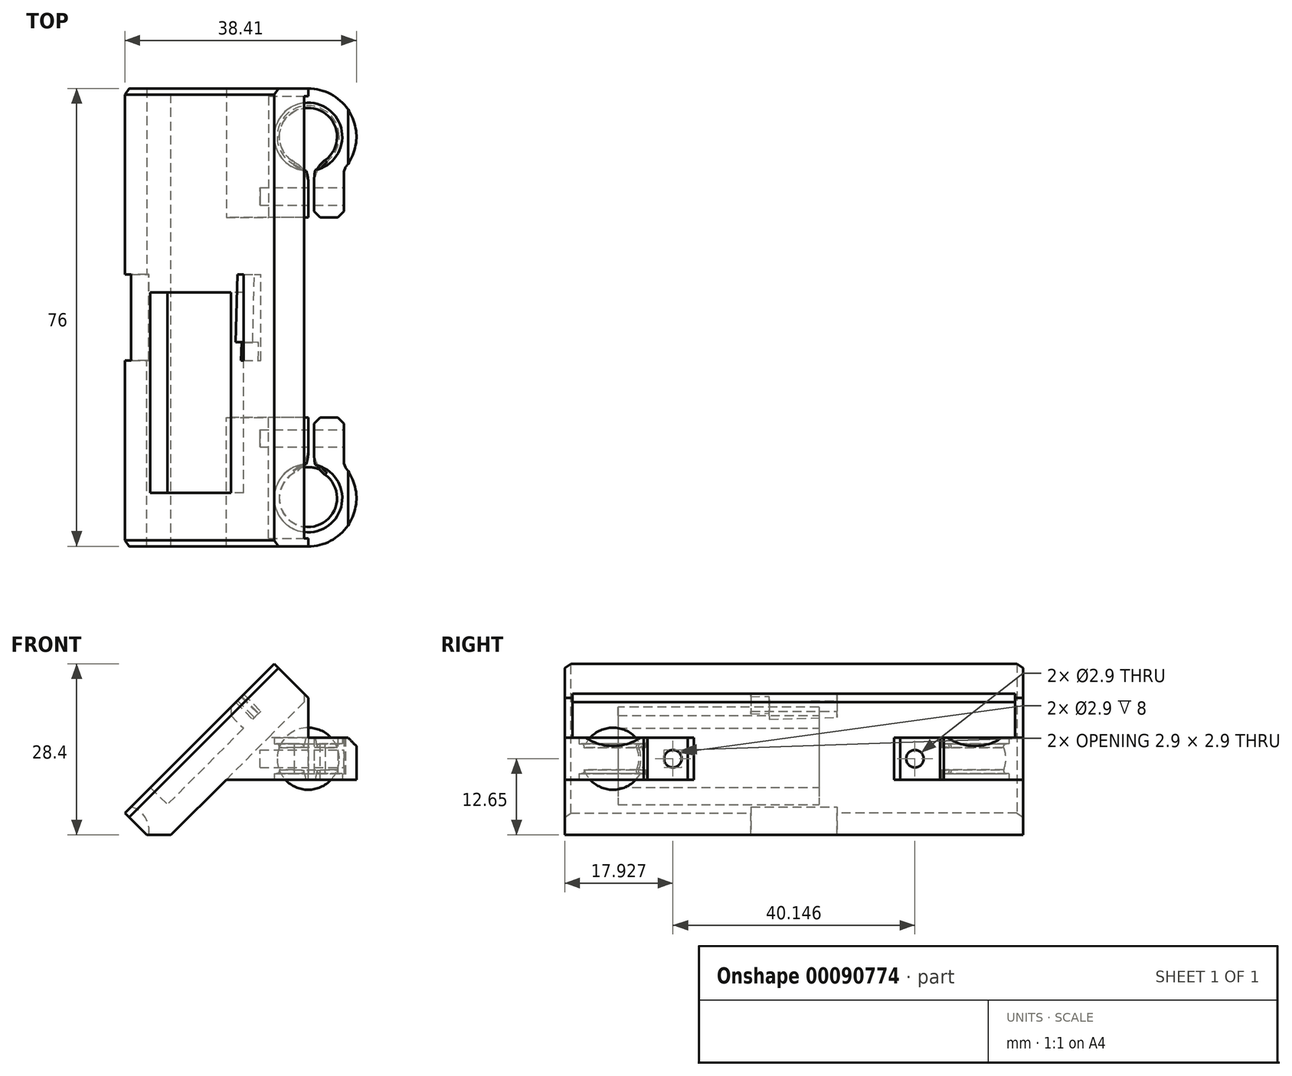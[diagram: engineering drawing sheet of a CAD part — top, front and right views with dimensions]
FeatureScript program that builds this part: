
annotation { "Feature Type Name" : "Feature", "Feature Type Description" : "" }
export const myFeature = defineFeature(function(context is Context, id is Id, definition is map)
    precondition{}
    {
        {
            assignVariable(context, id + "F0", {"name" : "balld", "anyValue" : 10});
        }
        {
            assignVariable(context, id + "F1", {"name" : "bushd", "anyValue" : 8});
        }
        {
            var Q0;
            Q0=qCreatedBy(makeId("Top.planeOp"),FACE);
            var sketch = newSketch(context, id + "F2", { "sketchPlane" : qUnion([Q0])});
            skLineSegment(sketch, "E0", {"start": v(0, -30) * mm, "end": v(0, 30) * mm});
            skCircle(sketch, "E1", {"center": v(0, -30) * mm, "radius": 5.15 * mm});
            skArc(sketch, "E2", {"start": v(0, -38) * mm, "mid": v(7.31, -33.24) * mm, "end": v(5.92, -24.62) * mm});
            skLineSegment(sketch, "E3", {"start": v(-5.15, -30) * mm, "end": v(5.15, -30) * mm});
            skLineSegment(sketch, "E4", {"start": v(-8, -30) * mm, "end": v(-8, 0) * mm});
            skLineSegment(sketch, "E5", {"start": v(-8, 0) * mm, "end": v(0, 0) * mm});
            skLineSegment(sketch, "E6", {"start": v(0, -16.62) * mm, "end": v(5.92, -16.62) * mm});
            skLineSegment(sketch, "E7", {"start": v(5.92, -16.62) * mm, "end": v(5.92, -24.62) * mm});
            skLineSegment(sketch, "E8", {"start": v(1, -30) * mm, "end": v(1, -16.62) * mm});
            skCircle(sketch, "E9.0", {"center": v(0, -30) * mm, "radius": 5.65 * mm});
            skLineSegment(sketch, "E10", {"start": v(-8, -30) * mm, "end": v(-8, -38) * mm});
            skLineSegment(sketch, "E11", {"start": v(-8, -38) * mm, "end": v(2.55, -38) * mm});
            skSolve(sketch);
        }
        {
            var Q0;
            Q0=makeQuery(id+"F2.imprint","IMPRINT",FACE,{"disambiguationData":[TD([[makeQuery(id+"F2.imprint","IMPRINT",EDGE,{"derivedFrom":sQuery(id+"F2.wireOp",EDGE,"E2")}),1.0]])]});
            var Q1;
            {var subQ0=sQuery(id+"F2.wireOp",EDGE,"E3");Q1=makeQuery(id+"F2.imprint","IMPRINT",FACE,{"disambiguationData":[TD([[makeQuery(id+"F2.imprint","IMPRINT",EDGE,{"derivedFrom":subQ0}),1.0]])]});}
            var Q2;
            {var subQ0=sQuery(id+"F2.wireOp",EDGE,"E3");Q2=makeQuery(id+"F2.imprint","IMPRINT",FACE,{"disambiguationData":[TD([[makeQuery(id+"F2.imprint","IMPRINT",EDGE,{"derivedFrom":subQ0}),-1.0]])]});}
            var Q3;
            {var subQ0=sQuery(id+"F2.wireOp",EDGE,"0A8tKCgS-ejaw-YyMs-Dn46-rruMUtFQQFLV");Q3=makeQuery(id+"F2.imprint","IMPRINT",FACE,{"disambiguationData":[TD([[makeQuery(id+"F2.imprint","IMPRINT",EDGE,{"derivedFrom":subQ0}),1.0]])]});}
            var Q4;
            {var subQ1=sQuery(id+"F2.wireOp",EDGE,"E1");var subQ8=sQuery(id+"F2.wireOp",EDGE,"E0");var subQ9=makeQuery(id+"F2.imprint","INTERSECT",VERTEX,{"derivedFrom":[subQ8,subQ1]});Q4=makeQuery(id+"F2.imprint","IMPRINT",FACE,{"disambiguationData":[TD([[makeQuery(id+"F2.imprint","IMPRINT",EDGE,{"disambiguationData":[TD([[subQ9,-1.0]])],"derivedFrom":subQ8}),1.0]])]});}
            extrude(context, id + "F3", {"entities" : qUnion([Q0, Q1, Q2, Q3, Q4]), "endBound" : BoundingType.SYMMETRIC, "depth" : (getVariable(context, 'balld') / 2) * mm});
        }
        {
            var Q0;
            {var subQ0=sQuery(id+"F2.wireOp",EDGE,"E3");var subQ1=sQuery(id+"F2.wireOp",EDGE,"E1");var subQ2=makeQuery(id+"F2.imprint","INTERSECT",VERTEX,{"disambiguationData":[OD(0.0)],"derivedFrom":[subQ1,subQ0]});Q0=makeQuery(id+"F2.imprint","IMPRINT",FACE,{"disambiguationData":[TD([[makeQuery(id+"F2.imprint","IMPRINT",EDGE,{"disambiguationData":[TD([[subQ2,-1.0]])],"derivedFrom":subQ1}),1.0]])]});}
            var Q1;
            Q1=sQuery(id+"F2.wireOp",EDGE,"E3");
            revolve(context, id + "F4", {"operationType" : NewBodyOperationType.REMOVE, "entities" : qUnion([Q0]), "axis" : qUnion([Q1]), "revolveType" : RevolveType.FULL, "oppositeDirection" : true});
        }
        {
            var Q0;
            Q0=makeQuery(id+"F2.imprint","IMPRINT",FACE,{"disambiguationData":[TD([[makeQuery(id+"F2.imprint","IMPRINT",EDGE,{"derivedFrom":sQuery(id+"F2.wireOp",EDGE,"E2")}),1.0]])]});
            extrude(context, id + "F5", {"entities" : qUnion([Q0]), "operationType" : NewBodyOperationType.ADD, "endBound" : BoundingType.SYMMETRIC, "depth" : 7 * mm});
        }
        {
            var Q0;
            {var subQ0=sQuery(id+"F2.wireOp",EDGE,"E3");var subQ1=sQuery(id+"F2.wireOp",EDGE,"E1");var subQ2=makeQuery(id+"F2.imprint","INTERSECT",VERTEX,{"disambiguationData":[OD(0.0)],"derivedFrom":[subQ1,subQ0]});Q0=makeQuery(id+"F2.imprint","IMPRINT",FACE,{"disambiguationData":[TD([[makeQuery(id+"F2.imprint","IMPRINT",EDGE,{"disambiguationData":[TD([[subQ2,-1.0]])],"derivedFrom":subQ1}),1.0]])]});}
            var Q1;
            Q1=sQuery(id+"F2.wireOp",EDGE,"E3");
            revolve(context, id + "F6", {"entities" : qUnion([Q0]), "axis" : qUnion([Q1]), "revolveType" : RevolveType.FULL});
        }
        {
            var Q0;
            Q0=makeQuery(id+"F4.boolean.opBoolean","INTERSECT",EDGE,{"derivedFrom":[makeQuery(id+"F3.opExtrude","SWEPT_FACE",FACE,{"disambiguationData":[OSD([sQuery(id+"F2.wireOp",EDGE,"E0")])]}),makeQuery(id+"F4.opRevolve","SWEPT_FACE",FACE,{"disambiguationData":[OSD([sQuery(id+"F2.wireOp",EDGE,"E1")])]})]});
            var Q1;
            Q1=makeQuery(id+"F4.boolean.opBoolean","INTERSECT",EDGE,{"derivedFrom":[makeQuery(id+"F3.opExtrude","SWEPT_FACE",FACE,{"disambiguationData":[OSD([sQuery(id+"F2.wireOp",EDGE,"E8")])]}),makeQuery(id+"F4.opRevolve","SWEPT_FACE",FACE,{"disambiguationData":[OSD([sQuery(id+"F2.wireOp",EDGE,"E1")])]})]});
            fillet(context, id + "F7", {"entities" : qUnion([Q0, Q1]), "radius" : 4 * mm, "tangentPropagation" : true, "allowEdgeOverflow" : false});
        }
        {
            var Q0;
            {var subQ0=sQuery(id+"F2.wireOp",EDGE,"E7");Q0=makeQuery(id+"F5.boolean.opBoolean","MERGE",FACE,{"derivedFrom":[makeQuery(id+"F3.opExtrude","SWEPT_FACE",FACE,{"disambiguationData":[OSD([subQ0])]}),makeQuery(id+"F5.opExtrude","SWEPT_FACE",FACE,{"disambiguationData":[OSD([subQ0])]})]});}
            var sketch = newSketch(context, id + "F8", { "sketchPlane" : qUnion([Q0])});
            skCircle(sketch, "E12", {"center": v(-20.07, 0) * mm, "radius": 1.45 * mm});
            skPoint(sketch, "E12.centerSnap0", {"position": v(-16.62, 0) * mm});
            skSolve(sketch);
        }
        {
            var Q0;
            Q0=makeQuery(id+"F8.imprint","IMPRINT",FACE,{"disambiguationData":[TD([[makeQuery(id+"F8.imprint","IMPRINT",EDGE,{"derivedFrom":sQuery(id+"F8.wireOp",EDGE,"E12")}),1.0]])]});
            extrude(context, id + "F9", {"entities" : qUnion([Q0]), "operationType" : NewBodyOperationType.REMOVE, "oppositeDirection" : true, "depth" : 25 * mm});
        }
        {
            var Q0;
            {var subQ0=sQuery(id+"F2.wireOp",EDGE,"E5");Q0=makeQuery(id+"F5.boolean.opBoolean","MERGE",FACE,{"derivedFrom":[makeQuery(id+"F3.opExtrude","SWEPT_FACE",FACE,{"disambiguationData":[OSD([subQ0])]}),makeQuery(id+"F5.opExtrude","SWEPT_FACE",FACE,{"disambiguationData":[OSD([subQ0])]})]});}
            var sketch = newSketch(context, id + "F10", { "sketchPlane" : qUnion([Q0])});
            skLineSegment(sketch, "E13", {"start": v(30.4, -9) * mm, "end": v(5.66, 15.75) * mm});
            skLineSegment(sketch, "E14", {"start": v(5.66, 15.75) * mm, "end": v(0, 10.1) * mm});
            skLineSegment(sketch, "E15", {"start": v(0, 10.1) * mm, "end": v(6.6, 3.5) * mm});
            skLineSegment(sketch, "E16", {"start": v(6.6, 3.5) * mm, "end": v(24.75, -14.65) * mm});
            skLineSegment(sketch, "E17", {"start": v(30.4, -9) * mm, "end": v(24.75, -14.65) * mm});
            skLineSegment(sketch, "E18", {"start": v(26.75, -12.65) * mm, "end": v(22.75, -12.65) * mm});
            skLineSegment(sketch, "E19", {"start": v(8, -3.5) * mm, "end": v(13.6, -3.5) * mm});
            skLineSegment(sketch, "E20", {"start": v(-8, -3.5) * mm, "end": v(-8, 3.5) * mm});
            skLineSegment(sketch, "E21", {"start": v(0, 10.1) * mm, "end": v(-10.1, 0) * mm});
            skLineSegment(sketch, "E22.0", {"start": v(-8, 3.5) * mm, "end": v(0, 3.5) * mm});
            skSolve(sketch);
        }
        {
            var Q0;
            {var subQ0=sQuery(id+"F10.wireOp",EDGE,"E14");Q0=makeQuery(id+"F10.imprint","IMPRINT",FACE,{"disambiguationData":[TD([[makeQuery(id+"F10.imprint","IMPRINT",EDGE,{"derivedFrom":subQ0}),1.0]])]});}
            var Q1;
            {var subQ0=sQuery(id+"F10.wireOp",EDGE,"ik6ux5z4-sAW3-eP5y-JmRx-WD4Mi1XPYjA4");var subQ5=sQuery(id+"F10.wireOp",EDGE,"E16");var subQ6=makeQuery(id+"F10.imprint","INTERSECT",VERTEX,{"derivedFrom":[subQ0,subQ5]});Q1=makeQuery(id+"F10.imprint","IMPRINT",FACE,{"disambiguationData":[TD([[makeQuery(id+"F10.imprint","IMPRINT",EDGE,{"disambiguationData":[TD([[subQ6,1.0]])],"derivedFrom":subQ5}),-1.0]])]});}
            var Q2;
            {var subQ0=sQuery(id+"F2.wireOp",EDGE,"E11");Q2=makeQuery(id+"F5.boolean.opBoolean","MERGE",FACE,{"derivedFrom":[makeQuery(id+"F3.opExtrude","SWEPT_FACE",FACE,{"disambiguationData":[OSD([subQ0])]}),makeQuery(id+"F5.opExtrude","SWEPT_FACE",FACE,{"disambiguationData":[OSD([subQ0])]})]});}
            extrude(context, id + "F11", {"entities" : qUnion([Q0, Q1]), "operationType" : NewBodyOperationType.ADD, "endBound" : BoundingType.UP_TO_SURFACE, "oppositeDirection" : true, "endBoundEntityFace" : qUnion([Q2]), "depth" : (30 + getVariable(context, 'bushd')) * mm});
        }
        {
            var Q0;
            {var subQ0=sQuery(id+"F2.wireOp",EDGE,"E5");var subQ3=makeQuery(id+"F5.opExtrude","CAP_EDGE",EDGE,{"disambiguationData":[OSD([subQ0])],"isStart":true});Q0=makeQuery(id+"F10.imprint","IMPRINT",FACE,{"disambiguationData":[TD([[makeQuery(id+"F10.imprint","IMPRINT",EDGE,{"derivedFrom":subQ3}),-1.0]])]});}
            var Q1;
            {var subQ0=sQuery(id+"F10.wireOp",EDGE,"ik6ux5z4-sAW3-eP5y-JmRx-WD4Mi1XPYjA4");var subQ5=sQuery(id+"F10.wireOp",EDGE,"E16");var subQ6=makeQuery(id+"F10.imprint","INTERSECT",VERTEX,{"derivedFrom":[subQ0,subQ5]});Q1=makeQuery(id+"F10.imprint","IMPRINT",FACE,{"disambiguationData":[TD([[makeQuery(id+"F10.imprint","IMPRINT",EDGE,{"disambiguationData":[TD([[subQ6,1.0]])],"derivedFrom":subQ5}),-1.0]])]});}
            var Q2;
            {var subQ0=sQuery(id+"F2.wireOp",EDGE,"E6");Q2=makeQuery(id+"F5.boolean.opBoolean","MERGE",FACE,{"derivedFrom":[makeQuery(id+"F3.opExtrude","SWEPT_FACE",FACE,{"disambiguationData":[OSD([subQ0])]}),makeQuery(id+"F5.opExtrude","SWEPT_FACE",FACE,{"disambiguationData":[OSD([subQ0])]})]});}
            extrude(context, id + "F12", {"entities" : qUnion([Q0, Q1]), "operationType" : NewBodyOperationType.REMOVE, "endBound" : BoundingType.UP_TO_SURFACE, "oppositeDirection" : true, "endBoundEntityFace" : qUnion([Q2]), "depth" : 25 * mm});
        }
        {
            var Q0;
            {var subQ0=sQuery(id+"F10.wireOp",EDGE,"E22.0");var subQ1=sQuery(id+"F10.wireOp",EDGE,"E20");var subQ2=makeQuery(id+"F10.imprint","INTERSECT",VERTEX,{"derivedFrom":[subQ1,subQ0]});Q0=makeQuery(id+"F10.imprint","IMPRINT",FACE,{"disambiguationData":[TD([[makeQuery(id+"F10.imprint","IMPRINT",EDGE,{"disambiguationData":[TD([[subQ2,1.0]])],"derivedFrom":subQ1}),-1.0]])]});}
            extrude(context, id + "F13", {"entities" : qUnion([Q0]), "operationType" : NewBodyOperationType.REMOVE, "oppositeDirection" : true, "depth" : 34.76 * mm});
        }
        {
            var Q0;
            {var subQ0=sQuery(id+"F2.wireOp",EDGE,"E11");Q0=makeQuery(id+"F11.boolean.opBoolean","MERGE",FACE,{"derivedFrom":[makeQuery(id+"F5.boolean.opBoolean","MERGE",FACE,{"derivedFrom":[makeQuery(id+"F3.opExtrude","SWEPT_FACE",FACE,{"disambiguationData":[OSD([subQ0])]}),makeQuery(id+"F5.opExtrude","SWEPT_FACE",FACE,{"disambiguationData":[OSD([subQ0])]})]}),makeQuery(id+"F11.opExtrude","CAP_FACE",FACE,{"disambiguationData":[OSD([sQuery(id+"F2.wireOp",EDGE,"E4"),sQuery(id+"F2.wireOp",EDGE,"E5"),sQuery(id+"F10.wireOp",EDGE,"ik6ux5z4-sAW3-eP5y-JmRx-WD4Mi1XPYjA4"),sQuery(id+"F10.wireOp",EDGE,"E13"),sQuery(id+"F10.wireOp",EDGE,"E14"),sQuery(id+"F10.wireOp",EDGE,"E15"),sQuery(id+"F10.wireOp",EDGE,"NVdRs6pZ-gfCu-PPoY-FiU9-BY5B9J22exEP")])],"isStart":false})]});}
            var sketch = newSketch(context, id + "F14", { "sketchPlane" : qUnion([Q0])});
            skLineSegment(sketch, "E23", {"start": v(0, 3.5) * mm, "end": v(0, 10.1) * mm});
            skSolve(sketch);
        }
        {
            var Q0;
            Q0=makeQuery(id+"F14.imprint","IMPRINT",FACE,{"disambiguationData":[TD([[makeQuery(id+"F14.imprint","IMPRINT",EDGE,{"derivedFrom":sQuery(id+"F14.wireOp",EDGE,"E23")}),1.0]])]});
            extrude(context, id + "F15", {"entities" : qUnion([Q0]), "operationType" : NewBodyOperationType.ADD, "oppositeDirection" : true, "depth" : 1.3 * mm});
        }
        {
            var Q0;
            Q0=makeQuery(id+"F4.boolean.opBoolean","INTERSECT",EDGE,{"derivedFrom":[makeQuery(id+"F3.opExtrude","CAP_FACE",FACE,{"disambiguationData":[OSD([sQuery(id+"F2.wireOp",EDGE,"E0"),sQuery(id+"F2.wireOp",EDGE,"E2"),sQuery(id+"F2.wireOp",EDGE,"E3"),sQuery(id+"F2.wireOp",EDGE,"E4"),sQuery(id+"F2.wireOp",EDGE,"E5"),sQuery(id+"F2.wireOp",EDGE,"E6"),sQuery(id+"F2.wireOp",EDGE,"E7"),sQuery(id+"F2.wireOp",EDGE,"E8")])],"isStart":true}),makeQuery(id+"F4.opRevolve","SWEPT_FACE",FACE,{"disambiguationData":[OSD([sQuery(id+"F2.wireOp",EDGE,"E1")])]})]});
            var Q1;
            Q1=makeQuery(id+"F4.boolean.opBoolean","INTERSECT",EDGE,{"derivedFrom":[makeQuery(id+"F3.opExtrude","CAP_FACE",FACE,{"disambiguationData":[OSD([sQuery(id+"F2.wireOp",EDGE,"E0"),sQuery(id+"F2.wireOp",EDGE,"E2"),sQuery(id+"F2.wireOp",EDGE,"E3"),sQuery(id+"F2.wireOp",EDGE,"E4"),sQuery(id+"F2.wireOp",EDGE,"E5"),sQuery(id+"F2.wireOp",EDGE,"E6"),sQuery(id+"F2.wireOp",EDGE,"E7"),sQuery(id+"F2.wireOp",EDGE,"E8")])],"isStart":false}),makeQuery(id+"F4.opRevolve","SWEPT_FACE",FACE,{"disambiguationData":[OSD([sQuery(id+"F2.wireOp",EDGE,"E1")])]})]});
            var Q2;
            Q2=makeQuery(id+"F11.opExtrude","SWEPT_EDGE",EDGE,{"disambiguationData":[OSD([sQuery(id+"F2.wireOp",EDGE,"E5"),sQuery(id+"F10.wireOp",EDGE,"E15"),sQuery(id+"F10.wireOp",EDGE,"E16")])]});
            var Q3;
            Q3=makeQuery(id+"F15.opExtrude","SWEPT_EDGE",EDGE,{"disambiguationData":[OSD([sQuery(id+"F2.wireOp",EDGE,"E2"),sQuery(id+"F2.wireOp",EDGE,"E11"),sQuery(id+"F14.wireOp",EDGE,"E23")])]});
            fillet(context, id + "F16", {"entities" : qUnion([Q0, Q1, Q2, Q3]), "radius" : 0.5 * mm, "tangentPropagation" : true, "allowEdgeOverflow" : false});
        }
        {
            var Q0;
            Q0=makeQuery(id+"F11.opExtrude","SWEPT_FACE",FACE,{"disambiguationData":[OSD([sQuery(id+"F10.wireOp",EDGE,"E13")])]});
            cPlane(context, id + "F17", {"entities" : qUnion([Q0]), "cplaneType" : CPlaneType.OFFSET, "offset" : 2 * mm, "oppositeDirection" : true, "width" : 150 * mm, "height" : 150 * mm});
        }
        {
            var Q0;
            Q0=qCreatedBy(id+"F17.planeOp",FACE);
            var sketch = newSketch(context, id + "F18", { "sketchPlane" : qUnion([Q0])});
            skLineSegment(sketch, "E24.bottom", {"start": v(7.14, -34.1) * mm, "end": v(-27.86, -34.1) * mm});
            skLineSegment(sketch, "E24.top", {"start": v(7.14, -25.9) * mm, "end": v(-27.86, -25.9) * mm});
            skLineSegment(sketch, "E24.left", {"start": v(7.14, -34.1) * mm, "end": v(7.14, -25.9) * mm});
            skLineSegment(sketch, "E24.right", {"start": v(-27.86, -34.1) * mm, "end": v(-27.86, -25.9) * mm});
            skPoint(sketch, "E24.middle", {"position": v(-10.36, -30) * mm});
            skPoint(sketch, "E24.middle.positionSnap0", {"position": v(-10.36, 0) * mm});
            skPoint(sketch, "E24.centerSnap0", {"position": v(-10.36, 0) * mm});
            skLineSegment(sketch, "E25", {"start": v(7.14, -30) * mm, "end": v(-27.86, -30) * mm});
            skLineSegment(sketch, "E26", {"start": v(7.14, -21.9) * mm, "end": v(-27.86, -21.9) * mm});
            skLineSegment(sketch, "E27.0.0", {"start": v(-27.86, -38) * mm, "end": v(7.14, -38) * mm});
            skLineSegment(sketch, "E27.0.1", {"start": v(7.14, -38) * mm, "end": v(7.14, 0) * mm});
            skLineSegment(sketch, "E27.0.2", {"start": v(7.14, 0) * mm, "end": v(-27.86, 0) * mm});
            skLineSegment(sketch, "E27.0.3", {"start": v(-27.86, 0) * mm, "end": v(-27.86, -38) * mm});
            skLineSegment(sketch, "E28", {"start": v(4.14, 0) * mm, "end": v(4.14, -21.9) * mm});
            skLineSegment(sketch, "E29", {"start": v(4.14, -4) * mm, "end": v(7.14, -4) * mm});
            skLineSegment(sketch, "E30", {"start": v(7.14, -4) * mm, "end": v(5.64, -4) * mm});
            skSolve(sketch);
        }
        {
            var Q0;
            {var subQ0=sQuery(id+"F18.wireOp",EDGE,"E24.top");Q0=makeQuery(id+"F18.imprint","IMPRINT",FACE,{"disambiguationData":[TD([[makeQuery(id+"F18.imprint","IMPRINT",EDGE,{"derivedFrom":subQ0}),1.0]])]});}
            var Q1;
            Q1=sQuery(id+"F18.wireOp",EDGE,"E25");
            revolve(context, id + "F19", {"operationType" : NewBodyOperationType.REMOVE, "entities" : qUnion([Q0]), "axis" : qUnion([Q1]), "revolveType" : RevolveType.FULL, "oppositeDirection" : true});
        }
        {
            var Q0;
            {var subQ3=sQuery(id+"F18.wireOp",EDGE,"E28");Q0=makeQuery(id+"F18.imprint","IMPRINT",FACE,{"disambiguationData":[TD([[makeQuery(id+"F18.imprint","IMPRINT",EDGE,{"derivedFrom":subQ3}),-1.0]])]});}
            var Q1;
            {var subQ5=sQuery(id+"F18.wireOp",EDGE,"E29");Q1=makeQuery(id+"F18.imprint","IMPRINT",FACE,{"disambiguationData":[TD([[makeQuery(id+"F18.imprint","IMPRINT",EDGE,{"derivedFrom":subQ5}),1.0]])]});}
            extrude(context, id + "F20", {"entities" : qUnion([Q0, Q1]), "operationType" : NewBodyOperationType.REMOVE, "depth" : 2 * mm, "hasSecondDirection" : true, "secondDirectionOppositeDirection" : true, "secondDirectionDepth" : 2 * mm});
        }
        {
            var Q0;
            Q0=makeQuery(id+"F3.opExtrude","SWEPT_BODY",BODY,{"disambiguationData":[OSD([sQuery(id+"F2.wireOp",EDGE,"E0"),sQuery(id+"F2.wireOp",EDGE,"E2"),sQuery(id+"F2.wireOp",EDGE,"E3"),sQuery(id+"F2.wireOp",EDGE,"E4"),sQuery(id+"F2.wireOp",EDGE,"E5"),sQuery(id+"F2.wireOp",EDGE,"E6"),sQuery(id+"F2.wireOp",EDGE,"E7"),sQuery(id+"F2.wireOp",EDGE,"E8"),sQuery(id+"F2.wireOp",EDGE,"E10"),sQuery(id+"F2.wireOp",EDGE,"E11")])]});
            var Q1;
            {var subQ0=sQuery(id+"F10.wireOp",EDGE,"E14");Q1=makeQuery(id+"F10.imprint","IMPRINT",FACE,{"disambiguationData":[TD([[makeQuery(id+"F10.imprint","IMPRINT",EDGE,{"derivedFrom":subQ0}),1.0]])]});}
            mirror(context, id + "F21", {"operationType" : NewBodyOperationType.ADD, "entities" : qUnion([Q0]), "mirrorPlane" : qUnion([Q1])});
        }
        {
            var Q0;
            {var subQ0=makeQuery(id+"F20.boolean.opBoolean","COPY",FACE,{"derivedFrom":makeQuery(id+"F20.opExtrude","CAP_FACE",FACE,{"disambiguationData":[OSD([sQuery(id+"F18.wireOp",EDGE,"E26"),sQuery(id+"F18.wireOp",EDGE,"E27.0.1"),sQuery(id+"F18.wireOp",EDGE,"E27.0.2"),sQuery(id+"F18.wireOp",EDGE,"E27.0.3")])],"isStart":true})});Q0=makeQuery(id+"F21.boolean.opBoolean","MERGE",FACE,{"derivedFrom":[subQ0,makeQuery(id+"F21.opPattern","COPY",FACE,{"derivedFrom":subQ0,"instanceName":"1"})]});}
            var sketch = newSketch(context, id + "F22", { "sketchPlane" : qUnion([Q0])});
            skLineSegment(sketch, "E31", {"start": v(7.14, 0) * mm, "end": v(-27.86, 0) * mm, "construction": true});
            skLineSegment(sketch, "E32", {"start": v(7.14, 0.7) * mm, "end": v(-24.81, 1.89) * mm});
            skLineSegment(sketch, "E33", {"start": v(7.14, -2) * mm, "end": v(-27.86, -0.7) * mm});
            skLineSegment(sketch, "E34", {"start": v(7.14, -0.6) * mm, "end": v(4.14, -0.49) * mm});
            skLineSegment(sketch, "E35", {"start": v(4.14, -0.49) * mm, "end": v(4.1, -1.89) * mm});
            skLineSegment(sketch, "E36.1.0", {"start": v(-27.86, 0.6) * mm, "end": v(-24.86, 0.49) * mm});
            skLineSegment(sketch, "E36.1.1", {"start": v(-24.86, 0.49) * mm, "end": v(-24.81, 1.89) * mm});
            skPoint(sketch, "E36.center", {"position": v(-10.36, 0) * mm});
            skLineSegment(sketch, "E37", {"start": v(-27.86, 4) * mm, "end": v(7.14, 4) * mm});
            skLineSegment(sketch, "E38.MirrorCS", {"start": v(-27.86, -4) * mm, "end": v(7.14, -4) * mm});
            skSolve(sketch);
        }
        {
            var Q0;
            {var subQ8=sQuery(id+"F22.wireOp",EDGE,"E37");Q0=makeQuery(id+"F22.imprint","IMPRINT",FACE,{"disambiguationData":[TD([[makeQuery(id+"F22.imprint","IMPRINT",EDGE,{"derivedFrom":subQ8}),-1.0]])]});}
            var Q1;
            {var subQ9=sQuery(id+"F22.wireOp",EDGE,"E36.1.0");Q1=makeQuery(id+"F22.imprint","IMPRINT",FACE,{"disambiguationData":[TD([[makeQuery(id+"F22.imprint","IMPRINT",EDGE,{"derivedFrom":subQ9}),1.0]])]});}
            var Q2;
            {var subQ0=sQuery(id+"F22.wireOp",EDGE,"E38.MirrorCS");Q2=makeQuery(id+"F22.imprint","IMPRINT",FACE,{"disambiguationData":[TD([[makeQuery(id+"F22.imprint","IMPRINT",EDGE,{"derivedFrom":subQ0}),1.0]])]});}
            var Q3;
            {var subQ5=sQuery(id+"F22.wireOp",EDGE,"E34");Q3=makeQuery(id+"F22.imprint","IMPRINT",FACE,{"disambiguationData":[TD([[makeQuery(id+"F22.imprint","IMPRINT",EDGE,{"derivedFrom":subQ5}),1.0]])]});}
            extrude(context, id + "F23", {"entities" : qUnion([Q0, Q1, Q2, Q3]), "operationType" : NewBodyOperationType.ADD, "depth" : 4 * mm});
        }
        {
            var Q0;
            Q0=makeQuery(id+"F20.boolean.opBoolean","COPY",EDGE,{"derivedFrom":makeQuery(id+"F20.opExtrude","CAP_EDGE",EDGE,{"disambiguationData":[OSD([sQuery(id+"F18.wireOp",EDGE,"E26")])],"isStart":false})});
            var Q1;
            Q1=makeQuery(id+"F11.opExtrude","CAP_EDGE",EDGE,{"disambiguationData":[OSD([sQuery(id+"F10.wireOp",EDGE,"E13")])],"isStart":false});
            var Q2;
            Q2=makeQuery(id+"F23.opExtrude","CAP_EDGE",EDGE,{"disambiguationData":[OSD([sQuery(id+"F22.wireOp",EDGE,"E38.MirrorCS")])],"isStart":false});
            var Q3;
            Q3=makeQuery(id+"F23.opExtrude","CAP_EDGE",EDGE,{"disambiguationData":[OSD([sQuery(id+"F22.wireOp",EDGE,"E37")])],"isStart":false});
            var Q4;
            Q4=makeQuery(id+"F21.opPattern","COPY",EDGE,{"derivedFrom":makeQuery(id+"F20.boolean.opBoolean","COPY",EDGE,{"derivedFrom":makeQuery(id+"F20.opExtrude","CAP_EDGE",EDGE,{"disambiguationData":[OSD([sQuery(id+"F18.wireOp",EDGE,"E26")])],"isStart":false})}),"instanceName":"1"});
            var Q5;
            Q5=makeQuery(id+"F21.opPattern","COPY",EDGE,{"derivedFrom":makeQuery(id+"F11.opExtrude","CAP_EDGE",EDGE,{"disambiguationData":[OSD([sQuery(id+"F10.wireOp",EDGE,"E13")])],"isStart":false}),"instanceName":"1"});
            var Q6;
            {var subQ0=makeQuery(id+"F15.boolean.opBoolean","SPLIT",EDGE,{"derivedFrom":makeQuery(id+"F11.opExtrude","SWEPT_EDGE",EDGE,{"disambiguationData":[OSD([sQuery(id+"F10.wireOp",EDGE,"E14"),sQuery(id+"F10.wireOp",EDGE,"E15")])]})});Q6=makeQuery(id+"F21.boolean.opBoolean","MERGE",EDGE,{"derivedFrom":[subQ0,makeQuery(id+"F21.opPattern","COPY",EDGE,{"derivedFrom":subQ0,"instanceName":"1"})]});}
            var Q7;
            {var subQ0=sQuery(id+"F2.wireOp",EDGE,"E7");var subQ1=sQuery(id+"F2.wireOp",EDGE,"E6");Q7=makeQuery(id+"F5.boolean.opBoolean","MERGE",EDGE,{"derivedFrom":[makeQuery(id+"F3.opExtrude","SWEPT_EDGE",EDGE,{"disambiguationData":[OSD([subQ1,subQ0])]}),makeQuery(id+"F5.opExtrude","SWEPT_EDGE",EDGE,{"disambiguationData":[OSD([subQ1,subQ0])]})]});}
            var Q8;
            {var subQ0=sQuery(id+"F2.wireOp",EDGE,"E8");var subQ1=sQuery(id+"F2.wireOp",EDGE,"E6");Q8=makeQuery(id+"F5.boolean.opBoolean","MERGE",EDGE,{"derivedFrom":[makeQuery(id+"F3.opExtrude","SWEPT_EDGE",EDGE,{"disambiguationData":[OSD([subQ1,subQ0])]}),makeQuery(id+"F5.opExtrude","SWEPT_EDGE",EDGE,{"disambiguationData":[OSD([subQ1,subQ0])]})]});}
            var Q9;
            Q9=makeQuery(id+"F12.boolean.opBoolean","COPY",EDGE,{"derivedFrom":makeQuery(id+"F12.opExtrude","CAP_EDGE",EDGE,{"disambiguationData":[OSD([sQuery(id+"F2.wireOp",EDGE,"E0"),sQuery(id+"F2.wireOp",EDGE,"E5")])],"isStart":false})});
            var Q10;
            {var subQ0=sQuery(id+"F2.wireOp",EDGE,"E7");var subQ1=sQuery(id+"F2.wireOp",EDGE,"E6");Q10=makeQuery(id+"F21.opPattern","COPY",EDGE,{"derivedFrom":makeQuery(id+"F5.boolean.opBoolean","MERGE",EDGE,{"derivedFrom":[makeQuery(id+"F3.opExtrude","SWEPT_EDGE",EDGE,{"disambiguationData":[OSD([subQ1,subQ0])]}),makeQuery(id+"F5.opExtrude","SWEPT_EDGE",EDGE,{"disambiguationData":[OSD([subQ1,subQ0])]})]}),"instanceName":"1"});}
            var Q11;
            {var subQ0=sQuery(id+"F2.wireOp",EDGE,"E8");var subQ1=sQuery(id+"F2.wireOp",EDGE,"E6");Q11=makeQuery(id+"F21.opPattern","COPY",EDGE,{"derivedFrom":makeQuery(id+"F5.boolean.opBoolean","MERGE",EDGE,{"derivedFrom":[makeQuery(id+"F3.opExtrude","SWEPT_EDGE",EDGE,{"disambiguationData":[OSD([subQ1,subQ0])]}),makeQuery(id+"F5.opExtrude","SWEPT_EDGE",EDGE,{"disambiguationData":[OSD([subQ1,subQ0])]})]}),"instanceName":"1"});}
            var Q12;
            Q12=makeQuery(id+"F21.opPattern","COPY",EDGE,{"derivedFrom":makeQuery(id+"F12.boolean.opBoolean","COPY",EDGE,{"derivedFrom":makeQuery(id+"F12.opExtrude","CAP_EDGE",EDGE,{"disambiguationData":[OSD([sQuery(id+"F2.wireOp",EDGE,"E0"),sQuery(id+"F2.wireOp",EDGE,"E5")])],"isStart":false})}),"instanceName":"1"});
            var Q13;
            {var subQ0=sQuery(id+"F2.wireOp",EDGE,"E7");var subQ1=sQuery(id+"F2.wireOp",EDGE,"E2");Q13=makeQuery(id+"F21.opPattern","COPY",EDGE,{"derivedFrom":makeQuery(id+"F5.boolean.opBoolean","MERGE",EDGE,{"derivedFrom":[makeQuery(id+"F3.opExtrude","SWEPT_EDGE",EDGE,{"disambiguationData":[OSD([subQ1,subQ0])]}),makeQuery(id+"F5.opExtrude","SWEPT_EDGE",EDGE,{"disambiguationData":[OSD([subQ1,subQ0])]})]}),"instanceName":"1"});}
            var Q14;
            {var subQ0=sQuery(id+"F2.wireOp",EDGE,"E7");var subQ1=sQuery(id+"F2.wireOp",EDGE,"E2");Q14=makeQuery(id+"F5.boolean.opBoolean","MERGE",EDGE,{"derivedFrom":[makeQuery(id+"F3.opExtrude","SWEPT_EDGE",EDGE,{"disambiguationData":[OSD([subQ1,subQ0])]}),makeQuery(id+"F5.opExtrude","SWEPT_EDGE",EDGE,{"disambiguationData":[OSD([subQ1,subQ0])]})]});}
            chamfer(context, id + "F24", {"entities" : qUnion([Q0, Q1, Q2, Q3, Q4, Q5, Q6, Q7, Q8, Q9, Q10, Q11, Q12, Q13, Q14]), "width" : 1 * mm, "tangentPropagation" : true});
        }
        {
            var Q0;
            Q0=makeQuery(id+"F20.boolean.opBoolean","COPY",FACE,{"derivedFrom":makeQuery(id+"F20.opExtrude","SWEPT_FACE",FACE,{"disambiguationData":[OSD([sQuery(id+"F18.wireOp",EDGE,"E28")])]})});
            extrude(context, id + "F25", {"entities" : qUnion([Q0]), "operationType" : NewBodyOperationType.REMOVE, "oppositeDirection" : true, "depth" : 25 * mm});
        }
    });
